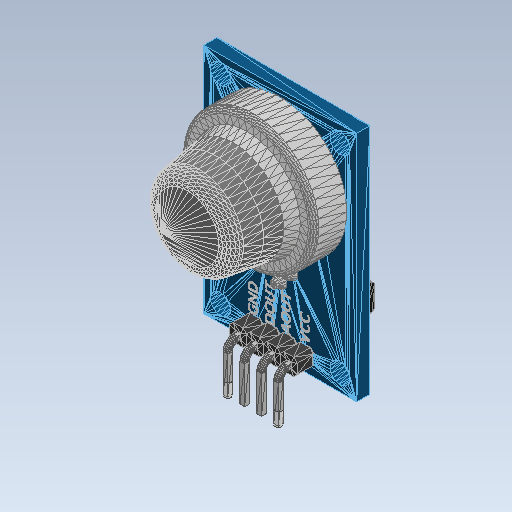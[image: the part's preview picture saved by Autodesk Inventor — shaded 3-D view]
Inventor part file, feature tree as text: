
AUTODESK INVENTOR PART (.ipt)
format: ipt  version: 2021 (Build 250183000, 183)  size: 328,192 bytes
history: native  units: mm
features: extrude x1, sketch x1, other x1
ambient origin geometry x8: Origin, YZ Plane, XZ Plane, XY Plane, X Axis, Y Axis, Z Axis, Center Point
bodies: Solid1 (feature_tree)
feature tree (3):
  extrude  "Extrusion1"  [1 undecoded]
  sketch  "Sketch1"  dims[d0=0.2mm d1=0.0mm]
  other  "MeshFeature1"
note: 1 required parameter value undecoded (feature->parameter linkage not recoverable at this tier; creation-order binding heuristic only, values carry confidence <= 0.55)
